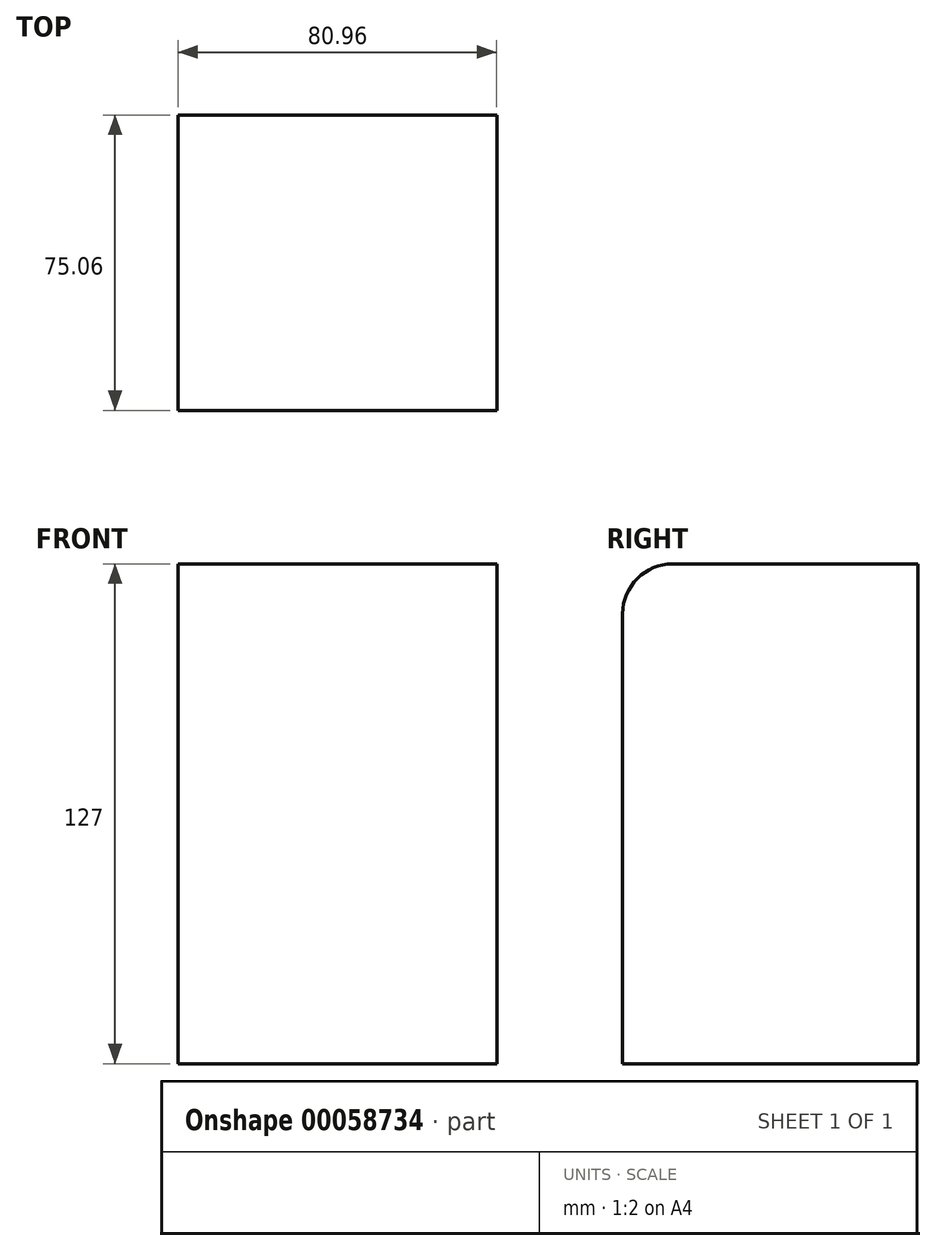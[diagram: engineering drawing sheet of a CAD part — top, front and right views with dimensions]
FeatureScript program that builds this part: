
annotation { "Feature Type Name" : "Feature", "Feature Type Description" : "" }
export const myFeature = defineFeature(function(context is Context, id is Id, definition is map)
    precondition{}
    {
        {
            var Q0;
            Q0=qCreatedBy(makeId("Top.planeOp"),FACE);
            var sketch = newSketch(context, id + "F0", { "sketchPlane" : qUnion([Q0])});
            skLineSegment(sketch, "E0.rect.bottom", {"start": v(40.48, 37.53) * mm, "end": v(-40.48, 37.53) * mm});
            skLineSegment(sketch, "E0.rect.top", {"start": v(40.48, -37.53) * mm, "end": v(-40.48, -37.53) * mm});
            skLineSegment(sketch, "E0.rect.left", {"start": v(40.48, 37.53) * mm, "end": v(40.48, -37.53) * mm});
            skLineSegment(sketch, "E0.rect.right", {"start": v(-40.48, 37.53) * mm, "end": v(-40.48, -37.53) * mm});
            skPoint(sketch, "E0.rect.middle", {"position": v(0, 0) * mm});
            skSolve(sketch);
        }
        {
            var Q0;
            Q0 = qSketchRegion(id + "F0", true);
            extrude(context, id + "F1", {"entities" : qUnion([Q0]), "depth" : 127 * mm});
        }
        {
            var Q0;
            Q0=makeQuery(id+"F1.opExtrude","CAP_EDGE",EDGE,{"disambiguationData":[OSD([sQuery(id+"F0.wireOp",EDGE,"E0.rect.top")])],"isStart":false});
            fillet(context, id + "F2", {"entities" : qUnion([Q0]), "radius" : 12.7 * mm, "tangentPropagation" : true, "allowEdgeOverflow" : false});
        }
    });
